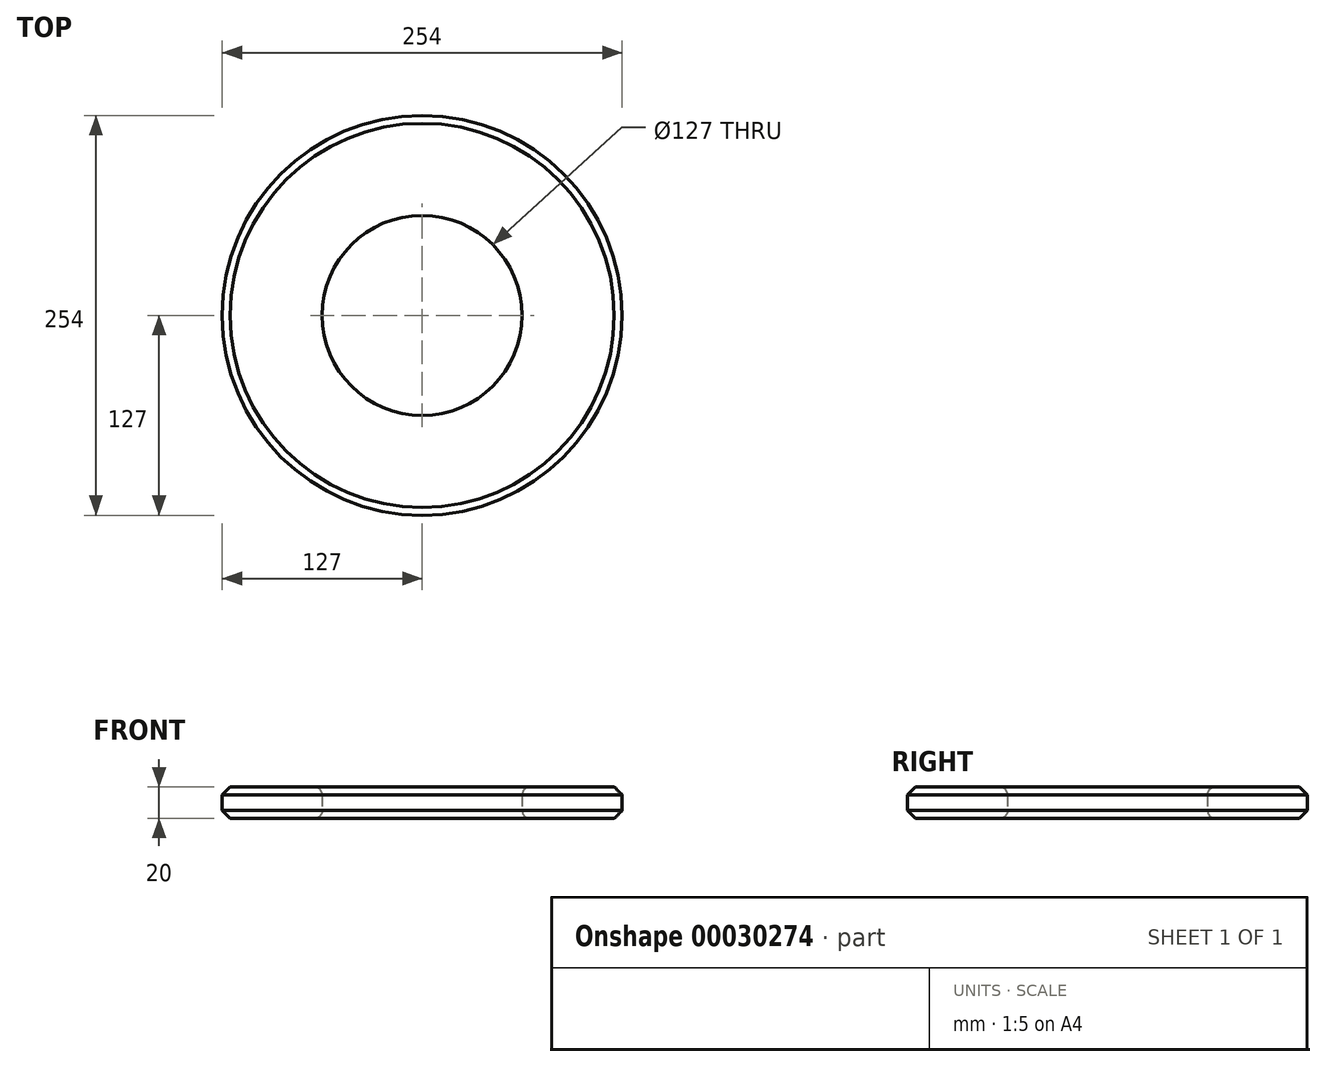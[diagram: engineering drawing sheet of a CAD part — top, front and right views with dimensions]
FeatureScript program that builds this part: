
annotation { "Feature Type Name" : "Feature", "Feature Type Description" : "" }
export const myFeature = defineFeature(function(context is Context, id is Id, definition is map)
    precondition{}
    {
        {
            var Q0;
            Q0=qCreatedBy(makeId("Top.planeOp"),FACE);
            var sketch = newSketch(context, id + "F0", { "sketchPlane" : qUnion([Q0])});
            skCircle(sketch, "E0", {"center": v(0, 0) * mm, "radius": 127 * mm});
            skCircle(sketch, "E1", {"center": v(0, 0) * mm, "radius": 63.5 * mm});
            skSolve(sketch);
        }
        {
            var Q0;
            Q0 = qSketchRegion(id + "F0", true);
            extrude(context, id + "F1", {"entities" : qUnion([Q0]), "depth" : 20 * mm});
        }
        {
            var Q0;
            Q0=makeQuery(id+"F1.opExtrude","CAP_EDGE",EDGE,{"disambiguationData":[OSD([sQuery(id+"F0.wireOp",EDGE,"E1")])],"isStart":false});
            fillet(context, id + "F2", {"entities" : qUnion([Q0]), "radius" : 5 * mm, "tangentPropagation" : true, "allowEdgeOverflow" : false});
        }
        {
            var Q0;
            Q0=makeQuery(id+"F1.opExtrude","CAP_EDGE",EDGE,{"disambiguationData":[OSD([sQuery(id+"F0.wireOp",EDGE,"E0")])],"isStart":false});
            chamfer(context, id + "F3", {"entities" : qUnion([Q0]), "width" : 5 * mm, "tangentPropagation" : true});
        }
        {
            var Q0;
            Q0=makeQuery(id+"F1.opExtrude","CAP_EDGE",EDGE,{"disambiguationData":[OSD([sQuery(id+"F0.wireOp",EDGE,"E0")])],"isStart":true});
            chamfer(context, id + "F4", {"entities" : qUnion([Q0]), "width" : 5 * mm, "tangentPropagation" : true});
        }
        {
            var Q0;
            Q0=makeQuery(id+"F1.opExtrude","CAP_EDGE",EDGE,{"disambiguationData":[OSD([sQuery(id+"F0.wireOp",EDGE,"E1")])],"isStart":true});
            fillet(context, id + "F5", {"entities" : qUnion([Q0]), "radius" : 5 * mm, "tangentPropagation" : true, "allowEdgeOverflow" : false});
        }
    });
